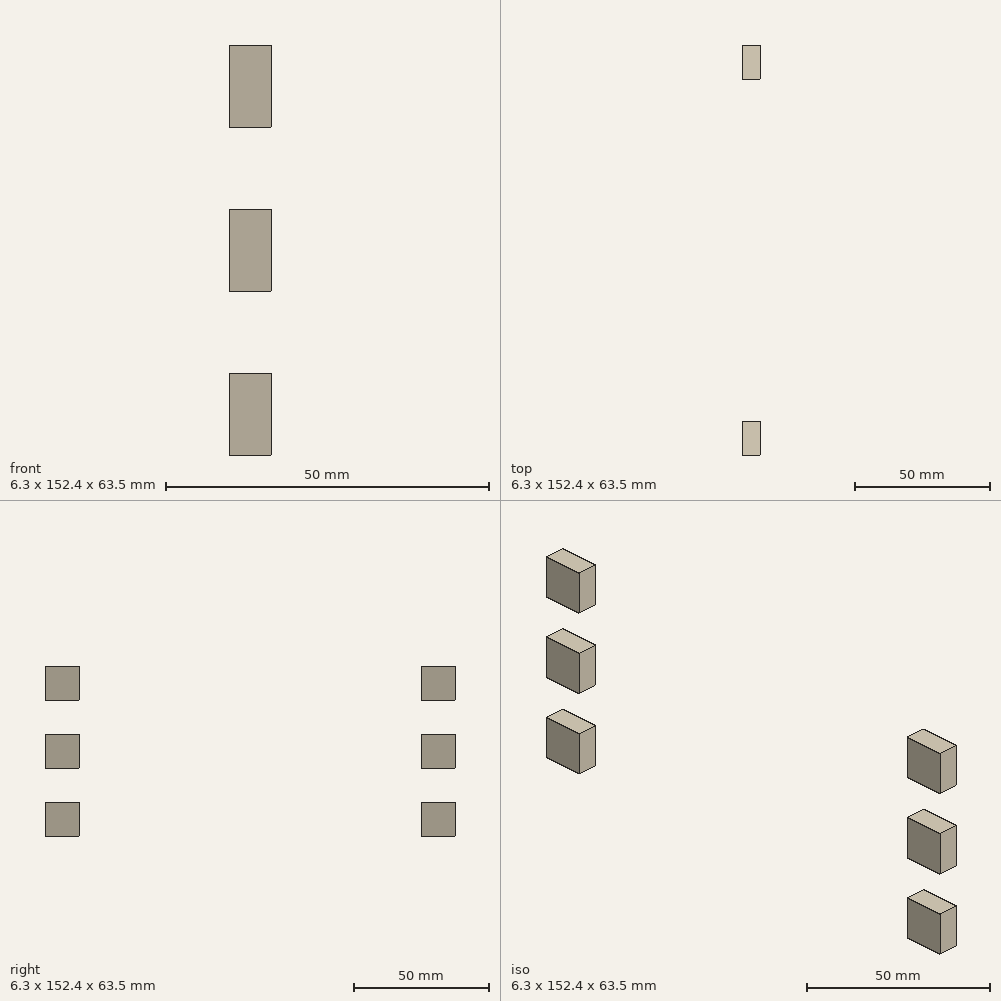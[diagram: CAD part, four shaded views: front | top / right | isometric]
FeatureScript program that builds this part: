
annotation { "Feature Type Name" : "Feature", "Feature Type Description" : "" }
export const myFeature = defineFeature(function(context is Context, id is Id, definition is map)
    precondition{}
    {
        {
            var Q0;
            Q0=qCreatedBy(makeId("Right.planeOp"),FACE);
            var sketch = newSketch(context, id + "F0", { "sketchPlane" : qUnion([Q0])});
            skLineSegment(sketch, "E0.bottom", {"start": v(-25.4, 12.7) * mm, "end": v(101.6, 12.7) * mm});
            skLineSegment(sketch, "E0.top", {"start": v(-25.4, -50.8) * mm, "end": v(101.6, -50.8) * mm});
            skLineSegment(sketch, "E0.right", {"start": v(101.6, 12.7) * mm, "end": v(101.6, -50.8) * mm});
            skLineSegment(sketch, "E1.bottom", {"start": v(12.7, 12.7) * mm, "end": v(63.5, 12.7) * mm});
            skLineSegment(sketch, "E1.top", {"start": v(12.7, 19.05) * mm, "end": v(63.5, 19.05) * mm});
            skLineSegment(sketch, "E1.left", {"start": v(12.7, 12.7) * mm, "end": v(12.7, 19.05) * mm});
            skLineSegment(sketch, "E1.right", {"start": v(63.5, 12.7) * mm, "end": v(63.5, 19.05) * mm});
            skLineSegment(sketch, "E2.bottom", {"start": v(12.7, -50.8) * mm, "end": v(63.5, -50.8) * mm});
            skLineSegment(sketch, "E2.top", {"start": v(12.7, -57.15) * mm, "end": v(63.5, -57.15) * mm});
            skLineSegment(sketch, "E2.left", {"start": v(12.7, -50.8) * mm, "end": v(12.7, -57.15) * mm});
            skLineSegment(sketch, "E2.right", {"start": v(63.5, -50.8) * mm, "end": v(63.5, -57.15) * mm});
            skLineSegment(sketch, "E3", {"start": v(-25.4, 12.7) * mm, "end": v(-25.4, -50.8) * mm});
            skLineSegment(sketch, "E4.bottom", {"start": v(-25.4, -12.7) * mm, "end": v(-38.1, -12.7) * mm});
            skLineSegment(sketch, "E4.top", {"start": v(-25.4, -25.4) * mm, "end": v(-38.1, -25.4) * mm});
            skLineSegment(sketch, "E4.left", {"start": v(-25.4, -12.7) * mm, "end": v(-25.4, -25.4) * mm});
            skLineSegment(sketch, "E4.right", {"start": v(-38.1, -12.7) * mm, "end": v(-38.1, -25.4) * mm});
            skLineSegment(sketch, "E5.bottom", {"start": v(-25.4, -38.1) * mm, "end": v(-38.1, -38.1) * mm});
            skLineSegment(sketch, "E5.top", {"start": v(-25.4, -50.8) * mm, "end": v(-38.1, -50.8) * mm});
            skLineSegment(sketch, "E5.left", {"start": v(-25.4, -38.1) * mm, "end": v(-25.4, -50.8) * mm});
            skLineSegment(sketch, "E5.right", {"start": v(-38.1, -38.1) * mm, "end": v(-38.1, -50.8) * mm});
            skLineSegment(sketch, "E6.bottom", {"start": v(-38.1, 12.7) * mm, "end": v(-25.4, 12.7) * mm});
            skLineSegment(sketch, "E6.top", {"start": v(-38.1, 0) * mm, "end": v(-25.4, 0) * mm});
            skLineSegment(sketch, "E6.left", {"start": v(-38.1, 12.7) * mm, "end": v(-38.1, 0) * mm});
            skLineSegment(sketch, "E6.right", {"start": v(-25.4, 12.7) * mm, "end": v(-25.4, 0) * mm});
            skLineSegment(sketch, "E7.bottom", {"start": v(114.3, -12.7) * mm, "end": v(101.6, -12.7) * mm});
            skLineSegment(sketch, "E7.top", {"start": v(114.3, -25.4) * mm, "end": v(101.6, -25.4) * mm});
            skLineSegment(sketch, "E7.left", {"start": v(114.3, -12.7) * mm, "end": v(114.3, -25.4) * mm});
            skLineSegment(sketch, "E7.right", {"start": v(101.6, -12.7) * mm, "end": v(101.6, -25.4) * mm});
            skLineSegment(sketch, "E8.bottom", {"start": v(114.3, -38.1) * mm, "end": v(101.6, -38.1) * mm});
            skLineSegment(sketch, "E8.top", {"start": v(114.3, -50.8) * mm, "end": v(101.6, -50.8) * mm});
            skLineSegment(sketch, "E8.left", {"start": v(114.3, -38.1) * mm, "end": v(114.3, -50.8) * mm});
            skLineSegment(sketch, "E8.right", {"start": v(101.6, -38.1) * mm, "end": v(101.6, -50.8) * mm});
            skLineSegment(sketch, "E9.bottom", {"start": v(101.6, 12.7) * mm, "end": v(114.3, 12.7) * mm});
            skLineSegment(sketch, "E9.top", {"start": v(101.6, 0) * mm, "end": v(114.3, 0) * mm});
            skLineSegment(sketch, "E9.left", {"start": v(101.6, 12.7) * mm, "end": v(101.6, 0) * mm});
            skLineSegment(sketch, "E9.right", {"start": v(114.3, 12.7) * mm, "end": v(114.3, 0) * mm});
            skSolve(sketch);
        }
        {
            var Q0;
            Q0=makeQuery(id+"F0.imprint","IMPRINT",FACE,{"disambiguationData":[TD([[makeQuery(id+"F0.imprint","IMPRINT",EDGE,{"derivedFrom":sQuery(id+"F0.wireOp",EDGE,"E6.bottom")}),-1.0]])]});
            var Q1;
            {var subQ1=sQuery(id+"F0.wireOp",EDGE,"E1.bottom");Q1=makeQuery(id+"F0.imprint","IMPRINT",FACE,{"disambiguationData":[TD([[makeQuery(id+"F0.imprint","IMPRINT",EDGE,{"derivedFrom":subQ1}),-1.0]])]});}
            var Q2;
            Q2=makeQuery(id+"F0.imprint","IMPRINT",FACE,{"disambiguationData":[TD([[makeQuery(id+"F0.imprint","IMPRINT",EDGE,{"derivedFrom":sQuery(id+"F0.wireOp",EDGE,"E4.bottom")}),1.0]])]});
            var Q3;
            Q3=makeQuery(id+"F0.imprint","IMPRINT",FACE,{"disambiguationData":[TD([[makeQuery(id+"F0.imprint","IMPRINT",EDGE,{"derivedFrom":sQuery(id+"F0.wireOp",EDGE,"E5.bottom")}),1.0]])]});
            var Q4;
            Q4=makeQuery(id+"F0.imprint","IMPRINT",FACE,{"disambiguationData":[TD([[makeQuery(id+"F0.imprint","IMPRINT",EDGE,{"derivedFrom":sQuery(id+"F0.wireOp",EDGE,"E2.bottom")}),-1.0]])]});
            var Q5;
            Q5=makeQuery(id+"F0.imprint","IMPRINT",FACE,{"disambiguationData":[TD([[makeQuery(id+"F0.imprint","IMPRINT",EDGE,{"derivedFrom":sQuery(id+"F0.wireOp",EDGE,"E1.bottom")}),1.0]])]});
            var Q6;
            Q6=makeQuery(id+"F0.imprint","IMPRINT",FACE,{"disambiguationData":[TD([[makeQuery(id+"F0.imprint","IMPRINT",EDGE,{"derivedFrom":sQuery(id+"F0.wireOp",EDGE,"E9.bottom")}),-1.0]])]});
            var Q7;
            Q7=makeQuery(id+"F0.imprint","IMPRINT",FACE,{"disambiguationData":[TD([[makeQuery(id+"F0.imprint","IMPRINT",EDGE,{"derivedFrom":sQuery(id+"F0.wireOp",EDGE,"E7.bottom")}),1.0]])]});
            var Q8;
            Q8=makeQuery(id+"F0.imprint","IMPRINT",FACE,{"disambiguationData":[TD([[makeQuery(id+"F0.imprint","IMPRINT",EDGE,{"derivedFrom":sQuery(id+"F0.wireOp",EDGE,"E8.bottom")}),1.0]])]});
            extrude(context, id + "F1", {"entities" : qUnion([Q0, Q1, Q2, Q3, Q4, Q5, Q6, Q7, Q8]), "depth" : 6.35 * mm, "offsetDistance" : 25.4 * mm});
        }
    });
